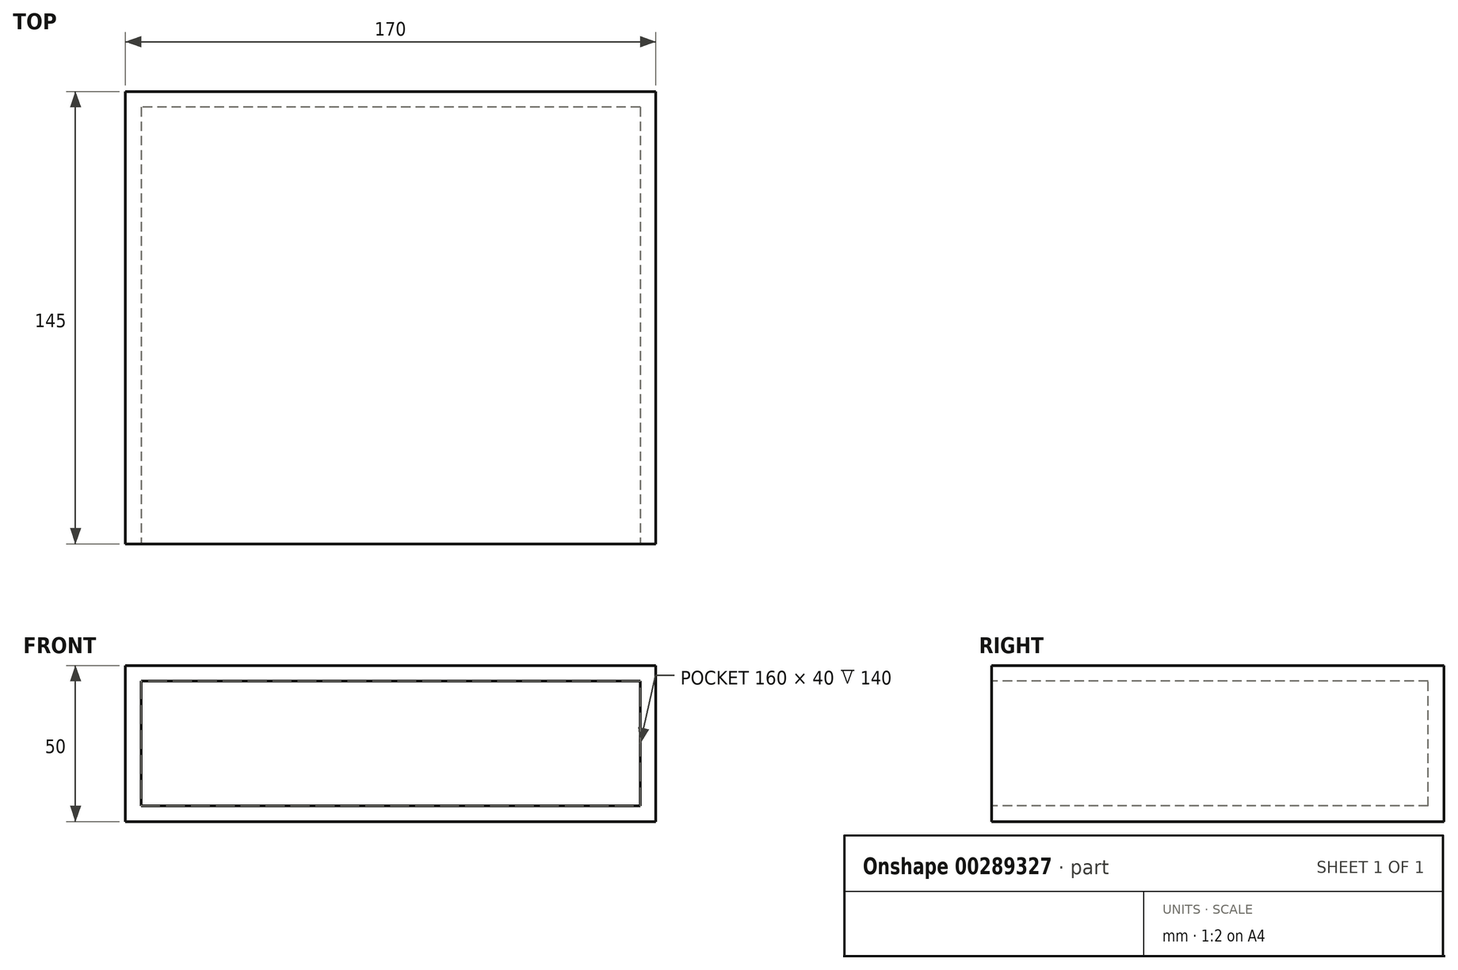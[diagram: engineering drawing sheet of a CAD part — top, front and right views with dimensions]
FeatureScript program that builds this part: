
annotation { "Feature Type Name" : "Feature", "Feature Type Description" : "" }
export const myFeature = defineFeature(function(context is Context, id is Id, definition is map)
    precondition{}
    {
        {
            var Q0;
            Q0=qCreatedBy(makeId("Front.planeOp"),FACE);
            var sketch = newSketch(context, id + "F0", { "sketchPlane" : qUnion([Q0]) });
            skLineSegment(sketch, "E0.bottom", {"start": v(80, -20) * mm, "end": v(-80, -20) * mm});
            skLineSegment(sketch, "E0.top", {"start": v(80, 20) * mm, "end": v(-80, 20) * mm});
            skLineSegment(sketch, "E0.left", {"start": v(80, -20) * mm, "end": v(80, 20) * mm});
            skLineSegment(sketch, "E0.right", {"start": v(-80, -20) * mm, "end": v(-80, 20) * mm});
            skPoint(sketch, "E0.middle", {"position": v(0, 0) * mm});
            skLineSegment(sketch, "E1.bottom", {"start": v(85, -25) * mm, "end": v(-85, -25) * mm});
            skLineSegment(sketch, "E1.top", {"start": v(85, 25) * mm, "end": v(-85, 25) * mm});
            skLineSegment(sketch, "E1.left", {"start": v(85, -25) * mm, "end": v(85, 25) * mm});
            skLineSegment(sketch, "E1.right", {"start": v(-85, -25) * mm, "end": v(-85, 25) * mm});
            skSolve(sketch);
        }
        {
            var Q0;
            Q0=makeQuery(id+"F0.imprint","IMPRINT",FACE,{"disambiguationData":[TD([[makeQuery(id+"F0.imprint","IMPRINT",EDGE,{"derivedFrom":sQuery(id+"F0.wireOp",EDGE,"E0.bottom")}),1.0]])]});
            var Q1;
            Q1=makeQuery(id+"F0.imprint","IMPRINT",FACE,{"disambiguationData":[TD([[makeQuery(id+"F0.imprint","IMPRINT",EDGE,{"derivedFrom":sQuery(id+"F0.wireOp",EDGE,"E0.bottom")}),-1.0]])]});
            extrude(context, id + "F1", {"entities" : qUnion([Q0, Q1]), "oppositeDirection" : true, "depth" : 145 * mm, "offsetDistance" : 25 * mm});
        }
        {
            var Q0;
            Q0=makeQuery(id+"F0.imprint","IMPRINT",FACE,{"disambiguationData":[TD([[makeQuery(id+"F0.imprint","IMPRINT",EDGE,{"derivedFrom":sQuery(id+"F0.wireOp",EDGE,"E0.bottom")}),-1.0]])]});
            extrude(context, id + "F2", {"entities" : qUnion([Q0]), "operationType" : NewBodyOperationType.REMOVE, "oppositeDirection" : true, "depth" : 140 * mm, "offsetDistance" : 25 * mm});
        }
    });
